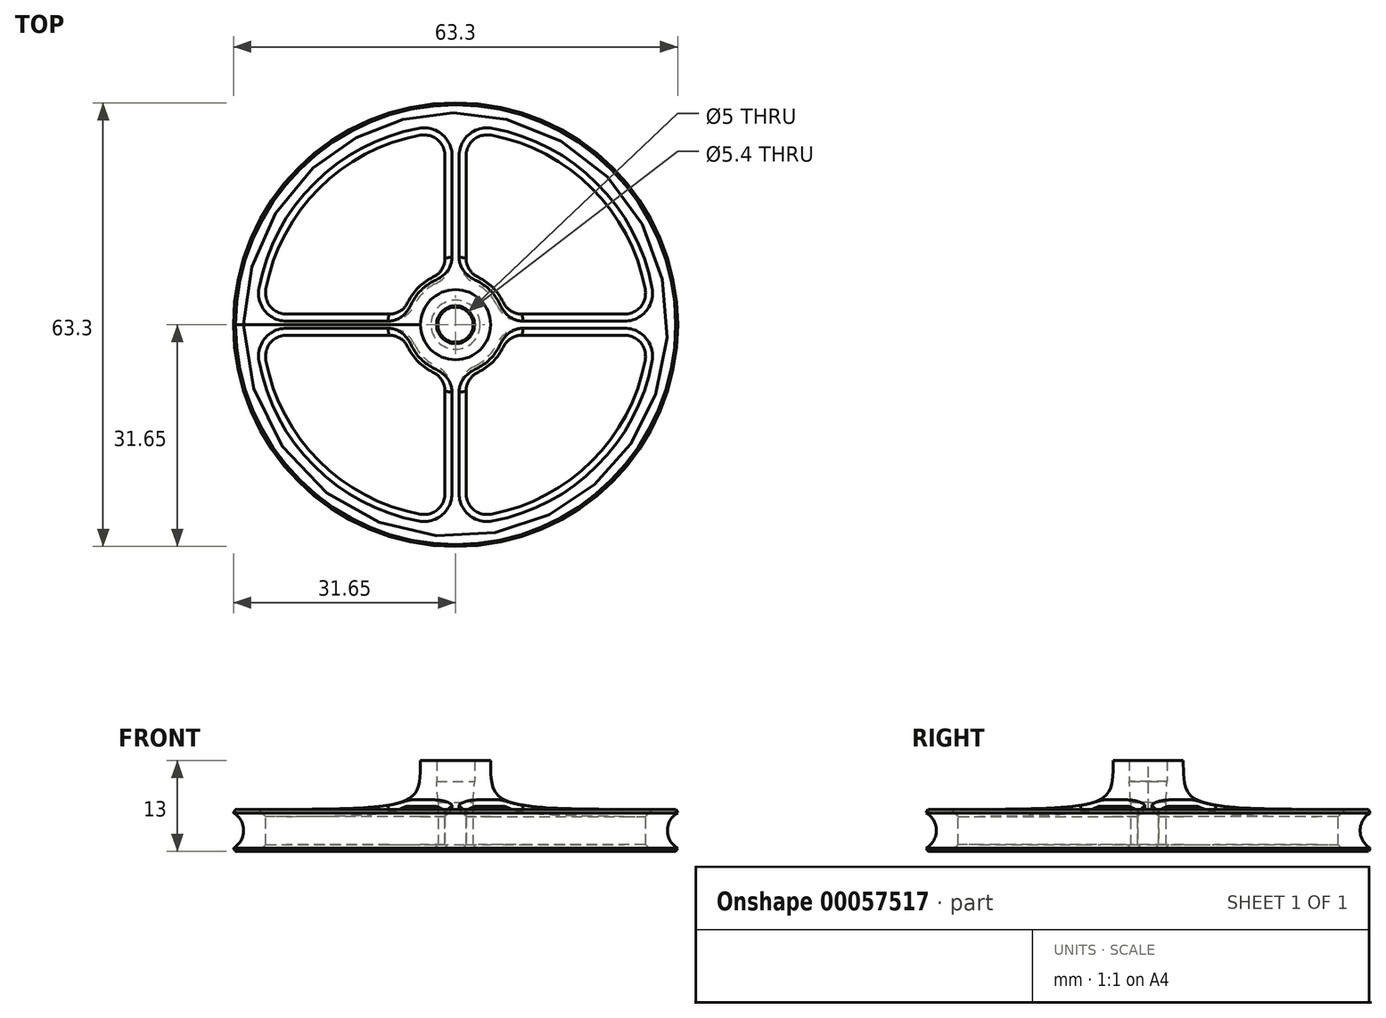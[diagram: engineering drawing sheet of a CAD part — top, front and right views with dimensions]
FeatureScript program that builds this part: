
annotation { "Feature Type Name" : "Feature", "Feature Type Description" : "" }
export const myFeature = defineFeature(function(context is Context, id is Id, definition is map)
    precondition{}
    {
        {
            var Q0;
            Q0=qCreatedBy(makeId("Front.planeOp"),FACE);
            var sketch = newSketch(context, id + "F0", { "sketchPlane" : qUnion([Q0])});
            skCircle(sketch, "E0", {"center": v(-33.1, 0) * mm, "radius": 2.9 * mm, "construction": true});
            skPoint(sketch, "E1", {"position": v(-30.2, 0) * mm});
            skPoint(sketch, "E2", {"position": v(-36, 0) * mm});
            skLineSegment(sketch, "E3", {"start": v(-31.65, 2.51) * mm, "end": v(-31.65, -2.51) * mm, "construction": true});
            skLineSegment(sketch, "E4", {"start": v(-31.65, -2.51) * mm, "end": v(-27.3, 0) * mm, "construction": true});
            skLineSegment(sketch, "E5", {"start": v(-27.3, 0) * mm, "end": v(-31.65, 2.51) * mm, "construction": true});
            skLineSegment(sketch, "E6", {"start": v(-31.65, -2.51) * mm, "end": v(-31.37, -3) * mm});
            skLineSegment(sketch, "E7", {"start": v(-31.37, -3) * mm, "end": v(0, -3) * mm, "construction": true});
            skLineSegment(sketch, "E8", {"start": v(0, -3) * mm, "end": v(0, 10) * mm, "construction": true});
            skLineSegment(sketch, "E9", {"start": v(0, 10) * mm, "end": v(-5, 10) * mm, "construction": true});
            skLineSegment(sketch, "E10", {"start": v(-5, 10) * mm, "end": v(-5, 3) * mm, "construction": true});
            skLineSegment(sketch, "E11", {"start": v(-5, 3) * mm, "end": v(-31.37, 3) * mm, "construction": true});
            skLineSegment(sketch, "E12", {"start": v(-31.37, 3) * mm, "end": v(-31.65, 2.51) * mm});
            skLineSegment(sketch, "E13", {"start": v(-2.7, 10) * mm, "end": v(-2.7, 7) * mm});
            skLineSegment(sketch, "E14", {"start": v(-2.7, 7) * mm, "end": v(-2.5, 4) * mm});
            skLineSegment(sketch, "E15", {"start": v(-2.5, 4) * mm, "end": v(-2.5, -3) * mm});
            skLineSegment(sketch, "E16", {"start": v(-2.7, 10) * mm, "end": v(-5, 10) * mm});
            skLineSegment(sketch, "E17", {"start": v(-2.5, -3) * mm, "end": v(-31.37, -3) * mm});
            skArc(sketch, "E18", {"start": v(-31.65, -2.51) * mm, "mid": v(-30.2, 0) * mm, "end": v(-31.65, 2.51) * mm});
            skFitSpline(sketch, "E19", {"points": [v(-31.37, 3) * mm, v(-5, 10) * mm], "startDerivative": vector(79.1, 0) * mm, "endDerivative": vector(0, 21) * mm});
            skSolve(sketch);
        }
        {
            var Q0;
            Q0 = qSketchRegion(id + "F0", true);
            var Q1;
            Q1=sQuery(id+"F0.wireOp",EDGE,"E8");
            revolve(context, id + "F1", {"entities" : qUnion([Q0]), "axis" : qUnion([Q1]), "revolveType" : RevolveType.FULL});
        }
        {
            var Q0;
            Q0=qCreatedBy(makeId("Top.planeOp"),FACE);
            var sketch = newSketch(context, id + "F2", { "sketchPlane" : qUnion([Q0])});
            skCircle(sketch, "E20", {"center": v(0, 0) * mm, "radius": 27.5 * mm, "construction": true});
            skCircle(sketch, "E21", {"center": v(0, 0) * mm, "radius": 7.5 * mm, "construction": true});
            skLineSegment(sketch, "E22", {"start": v(-1.5, 7.35) * mm, "end": v(0, 0) * mm, "construction": true});
            skLineSegment(sketch, "E23", {"start": v(1.5, 7.35) * mm, "end": v(0, 0) * mm, "construction": true});
            skLineSegment(sketch, "E24", {"start": v(-7.35, 1.5) * mm, "end": v(0, 0) * mm, "construction": true});
            skLineSegment(sketch, "E25", {"start": v(-7.35, -1.5) * mm, "end": v(0, 0) * mm, "construction": true});
            skLineSegment(sketch, "E26", {"start": v(-1.5, -7.35) * mm, "end": v(0, 0) * mm, "construction": true});
            skLineSegment(sketch, "E27", {"start": v(0, 0) * mm, "end": v(1.5, -7.35) * mm, "construction": true});
            skLineSegment(sketch, "E28", {"start": v(7.35, 1.5) * mm, "end": v(0, 0) * mm, "construction": true});
            skLineSegment(sketch, "E29", {"start": v(0, 0) * mm, "end": v(7.35, -1.5) * mm, "construction": true});
            skLineSegment(sketch, "E30", {"start": v(-1.5, 7.35) * mm, "end": v(-1.5, 27.46) * mm});
            skLineSegment(sketch, "E31", {"start": v(1.5, 7.35) * mm, "end": v(1.5, 27.46) * mm});
            skLineSegment(sketch, "E32", {"start": v(-1.5, -7.35) * mm, "end": v(-1.5, -27.46) * mm});
            skLineSegment(sketch, "E33", {"start": v(1.5, -7.35) * mm, "end": v(1.5, -27.46) * mm});
            skLineSegment(sketch, "E34", {"start": v(-7.35, 1.5) * mm, "end": v(-27.46, 1.5) * mm});
            skLineSegment(sketch, "E35", {"start": v(-7.35, -1.5) * mm, "end": v(-27.46, -1.5) * mm});
            skLineSegment(sketch, "E36", {"start": v(7.35, 1.5) * mm, "end": v(27.46, 1.5) * mm});
            skLineSegment(sketch, "E37", {"start": v(7.35, -1.5) * mm, "end": v(27.46, -1.5) * mm});
            skArc(sketch, "E38", {"start": v(-1.5, 27.46) * mm, "mid": v(-19.45, 19.45) * mm, "end": v(-27.46, 1.5) * mm});
            skArc(sketch, "E39", {"start": v(-1.5, 7.35) * mm, "mid": v(-5.3, 5.3) * mm, "end": v(-7.35, 1.5) * mm});
            skArc(sketch, "E40", {"start": v(-27.46, -1.5) * mm, "mid": v(-19.45, -19.45) * mm, "end": v(-1.5, -27.46) * mm});
            skArc(sketch, "E41", {"start": v(-7.35, -1.5) * mm, "mid": v(-5.3, -5.3) * mm, "end": v(-1.5, -7.35) * mm});
            skArc(sketch, "E42", {"start": v(1.5, -7.35) * mm, "mid": v(5.3, -5.3) * mm, "end": v(7.35, -1.5) * mm});
            skArc(sketch, "E43", {"start": v(1.5, -27.46) * mm, "mid": v(19.45, -19.45) * mm, "end": v(27.46, -1.5) * mm});
            skArc(sketch, "E44", {"start": v(27.46, 1.5) * mm, "mid": v(19.45, 19.45) * mm, "end": v(1.5, 27.46) * mm});
            skArc(sketch, "E45", {"start": v(7.35, 1.5) * mm, "mid": v(5.3, 5.3) * mm, "end": v(1.5, 7.35) * mm});
            skSolve(sketch);
        }
        {
            var Q0;
            Q0 = qSketchRegion(id + "F2", true);
            extrude(context, id + "F3", {"entities" : qUnion([Q0]), "operationType" : NewBodyOperationType.REMOVE, "endBound" : BoundingType.THROUGH_ALL, "oppositeDirection" : true, "depth" : 25 * mm, "hasSecondDirection" : true, "secondDirectionBound" : SecondDirectionBoundingType.THROUGH_ALL, "secondDirectionOppositeDirection" : false, "secondDirectionDepth" : 25 * mm});
        }
        {
            var Q0;
            Q0=makeQuery(id+"F3.boolean.opBoolean","COPY",EDGE,{"derivedFrom":makeQuery(id+"F3.opExtrude","SWEPT_EDGE",EDGE,{"disambiguationData":[OSD([sQuery(id+"F2.wireOp",EDGE,"E34"),sQuery(id+"F2.wireOp",EDGE,"E39")])]})});
            var Q1;
            Q1=makeQuery(id+"F3.boolean.opBoolean","COPY",EDGE,{"derivedFrom":makeQuery(id+"F3.opExtrude","SWEPT_EDGE",EDGE,{"disambiguationData":[OSD([sQuery(id+"F2.wireOp",EDGE,"E30"),sQuery(id+"F2.wireOp",EDGE,"E39")])]})});
            var Q2;
            Q2=makeQuery(id+"F3.boolean.opBoolean","COPY",EDGE,{"derivedFrom":makeQuery(id+"F3.opExtrude","SWEPT_EDGE",EDGE,{"disambiguationData":[OSD([sQuery(id+"F2.wireOp",EDGE,"E30"),sQuery(id+"F2.wireOp",EDGE,"E38")])]})});
            var Q3;
            Q3=makeQuery(id+"F3.boolean.opBoolean","COPY",EDGE,{"derivedFrom":makeQuery(id+"F3.opExtrude","SWEPT_EDGE",EDGE,{"disambiguationData":[OSD([sQuery(id+"F2.wireOp",EDGE,"E37"),sQuery(id+"F2.wireOp",EDGE,"E43")])]})});
            var Q4;
            Q4=makeQuery(id+"F3.boolean.opBoolean","COPY",EDGE,{"derivedFrom":makeQuery(id+"F3.opExtrude","SWEPT_EDGE",EDGE,{"disambiguationData":[OSD([sQuery(id+"F2.wireOp",EDGE,"E32"),sQuery(id+"F2.wireOp",EDGE,"E41")])]})});
            var Q5;
            Q5=makeQuery(id+"F3.boolean.opBoolean","COPY",EDGE,{"derivedFrom":makeQuery(id+"F3.opExtrude","SWEPT_EDGE",EDGE,{"disambiguationData":[OSD([sQuery(id+"F2.wireOp",EDGE,"E35"),sQuery(id+"F2.wireOp",EDGE,"E41")])]})});
            var Q6;
            Q6=makeQuery(id+"F3.boolean.opBoolean","COPY",EDGE,{"derivedFrom":makeQuery(id+"F3.opExtrude","SWEPT_EDGE",EDGE,{"disambiguationData":[OSD([sQuery(id+"F2.wireOp",EDGE,"E34"),sQuery(id+"F2.wireOp",EDGE,"E38")])]})});
            var Q7;
            Q7=makeQuery(id+"F3.boolean.opBoolean","COPY",EDGE,{"derivedFrom":makeQuery(id+"F3.opExtrude","SWEPT_EDGE",EDGE,{"disambiguationData":[OSD([sQuery(id+"F2.wireOp",EDGE,"E36"),sQuery(id+"F2.wireOp",EDGE,"E45")])]})});
            var Q8;
            Q8=makeQuery(id+"F3.boolean.opBoolean","COPY",EDGE,{"derivedFrom":makeQuery(id+"F3.opExtrude","SWEPT_EDGE",EDGE,{"disambiguationData":[OSD([sQuery(id+"F2.wireOp",EDGE,"E31"),sQuery(id+"F2.wireOp",EDGE,"E45")])]})});
            var Q9;
            Q9=makeQuery(id+"F3.boolean.opBoolean","COPY",EDGE,{"derivedFrom":makeQuery(id+"F3.opExtrude","SWEPT_EDGE",EDGE,{"disambiguationData":[OSD([sQuery(id+"F2.wireOp",EDGE,"E33"),sQuery(id+"F2.wireOp",EDGE,"E43")])]})});
            var Q10;
            Q10=makeQuery(id+"F3.boolean.opBoolean","COPY",EDGE,{"derivedFrom":makeQuery(id+"F3.opExtrude","SWEPT_EDGE",EDGE,{"disambiguationData":[OSD([sQuery(id+"F2.wireOp",EDGE,"E37"),sQuery(id+"F2.wireOp",EDGE,"E42")])]})});
            var Q11;
            Q11=makeQuery(id+"F3.boolean.opBoolean","COPY",EDGE,{"derivedFrom":makeQuery(id+"F3.opExtrude","SWEPT_EDGE",EDGE,{"disambiguationData":[OSD([sQuery(id+"F2.wireOp",EDGE,"E33"),sQuery(id+"F2.wireOp",EDGE,"E42")])]})});
            var Q12;
            Q12=makeQuery(id+"F3.boolean.opBoolean","COPY",EDGE,{"derivedFrom":makeQuery(id+"F3.opExtrude","SWEPT_EDGE",EDGE,{"disambiguationData":[OSD([sQuery(id+"F2.wireOp",EDGE,"E31"),sQuery(id+"F2.wireOp",EDGE,"E44")])]})});
            var Q13;
            Q13=makeQuery(id+"F3.boolean.opBoolean","COPY",EDGE,{"derivedFrom":makeQuery(id+"F3.opExtrude","SWEPT_EDGE",EDGE,{"disambiguationData":[OSD([sQuery(id+"F2.wireOp",EDGE,"E36"),sQuery(id+"F2.wireOp",EDGE,"E44")])]})});
            var Q14;
            Q14=makeQuery(id+"F3.boolean.opBoolean","COPY",EDGE,{"derivedFrom":makeQuery(id+"F3.opExtrude","SWEPT_EDGE",EDGE,{"disambiguationData":[OSD([sQuery(id+"F2.wireOp",EDGE,"E32"),sQuery(id+"F2.wireOp",EDGE,"E40")])]})});
            var Q15;
            Q15=makeQuery(id+"F3.boolean.opBoolean","COPY",EDGE,{"derivedFrom":makeQuery(id+"F3.opExtrude","SWEPT_EDGE",EDGE,{"disambiguationData":[OSD([sQuery(id+"F2.wireOp",EDGE,"E35"),sQuery(id+"F2.wireOp",EDGE,"E40")])]})});
            fillet(context, id + "F4", {"entities" : qUnion([Q0, Q1, Q2, Q3, Q4, Q5, Q6, Q7, Q8, Q9, Q10, Q11, Q12, Q13, Q14, Q15]), "radius" : 3 * mm, "tangentPropagation" : true, "allowEdgeOverflow" : false});
        }
        {
            var Q0;
            Q0=makeQuery(id+"F3.boolean.opBoolean","INTERSECT",EDGE,{"derivedFrom":[makeQuery(id+"F1.opRevolve","SWEPT_FACE",FACE,{"disambiguationData":[OSD([sQuery(id+"F0.wireOp",EDGE,"E17")])]}),makeQuery(id+"F3.opExtrude","SWEPT_FACE",FACE,{"disambiguationData":[OSD([sQuery(id+"F2.wireOp",EDGE,"E32")])]})]});
            var Q1;
            Q1=makeQuery(id+"F3.boolean.opBoolean","INTERSECT",EDGE,{"derivedFrom":[makeQuery(id+"F1.opRevolve","SWEPT_FACE",FACE,{"disambiguationData":[OSD([sQuery(id+"F0.wireOp",EDGE,"E17")])]}),makeQuery(id+"F3.opExtrude","SWEPT_FACE",FACE,{"disambiguationData":[OSD([sQuery(id+"F2.wireOp",EDGE,"E33")])]})]});
            var Q2;
            Q2=makeQuery(id+"F3.boolean.opBoolean","INTERSECT",EDGE,{"derivedFrom":[makeQuery(id+"F1.opRevolve","SWEPT_FACE",FACE,{"disambiguationData":[OSD([sQuery(id+"F0.wireOp",EDGE,"E17")])]}),makeQuery(id+"F3.opExtrude","SWEPT_FACE",FACE,{"disambiguationData":[OSD([sQuery(id+"F2.wireOp",EDGE,"E45")])]})]});
            var Q3;
            Q3=makeQuery(id+"F3.boolean.opBoolean","INTERSECT",EDGE,{"derivedFrom":[makeQuery(id+"F1.opRevolve","SWEPT_FACE",FACE,{"disambiguationData":[OSD([sQuery(id+"F0.wireOp",EDGE,"E17")])]}),makeQuery(id+"F3.opExtrude","SWEPT_FACE",FACE,{"disambiguationData":[OSD([sQuery(id+"F2.wireOp",EDGE,"E39")])]})]});
            var Q4;
            Q4=makeQuery(id+"F1.opRevolve","SWEPT_EDGE",EDGE,{"disambiguationData":[OSD([sQuery(id+"F0.wireOp",EDGE,"E15"),sQuery(id+"F0.wireOp",EDGE,"E17")])]});
            var Q5;
            Q5=makeQuery(id+"F3.boolean.opBoolean","INTERSECT",EDGE,{"derivedFrom":[makeQuery(id+"F1.opRevolve","SWEPT_FACE",FACE,{"disambiguationData":[OSD([sQuery(id+"F0.wireOp",EDGE,"E19")])]}),makeQuery(id+"F3.opExtrude","SWEPT_FACE",FACE,{"disambiguationData":[OSD([sQuery(id+"F2.wireOp",EDGE,"E36")])]})]});
            var Q6;
            Q6=makeQuery(id+"F3.boolean.opBoolean","INTERSECT",EDGE,{"derivedFrom":[makeQuery(id+"F1.opRevolve","SWEPT_FACE",FACE,{"disambiguationData":[OSD([sQuery(id+"F0.wireOp",EDGE,"E19")])]}),makeQuery(id+"F3.opExtrude","SWEPT_FACE",FACE,{"disambiguationData":[OSD([sQuery(id+"F2.wireOp",EDGE,"E30")])]})]});
            var Q7;
            Q7=makeQuery(id+"F3.boolean.opBoolean","INTERSECT",EDGE,{"derivedFrom":[makeQuery(id+"F1.opRevolve","SWEPT_FACE",FACE,{"disambiguationData":[OSD([sQuery(id+"F0.wireOp",EDGE,"E19")])]}),makeQuery(id+"F3.opExtrude","SWEPT_FACE",FACE,{"disambiguationData":[OSD([sQuery(id+"F2.wireOp",EDGE,"E40")])]})]});
            var Q8;
            Q8=makeQuery(id+"F3.boolean.opBoolean","INTERSECT",EDGE,{"derivedFrom":[makeQuery(id+"F1.opRevolve","SWEPT_FACE",FACE,{"disambiguationData":[OSD([sQuery(id+"F0.wireOp",EDGE,"E19")])]}),makeQuery(id+"F3.opExtrude","SWEPT_FACE",FACE,{"disambiguationData":[OSD([sQuery(id+"F2.wireOp",EDGE,"E43")])]})]});
            chamfer(context, id + "F5", {"entities" : qUnion([Q0, Q1, Q2, Q3, Q4, Q5, Q6, Q7, Q8]), "width" : 1 * mm, "tangentPropagation" : true});
        }
    });
